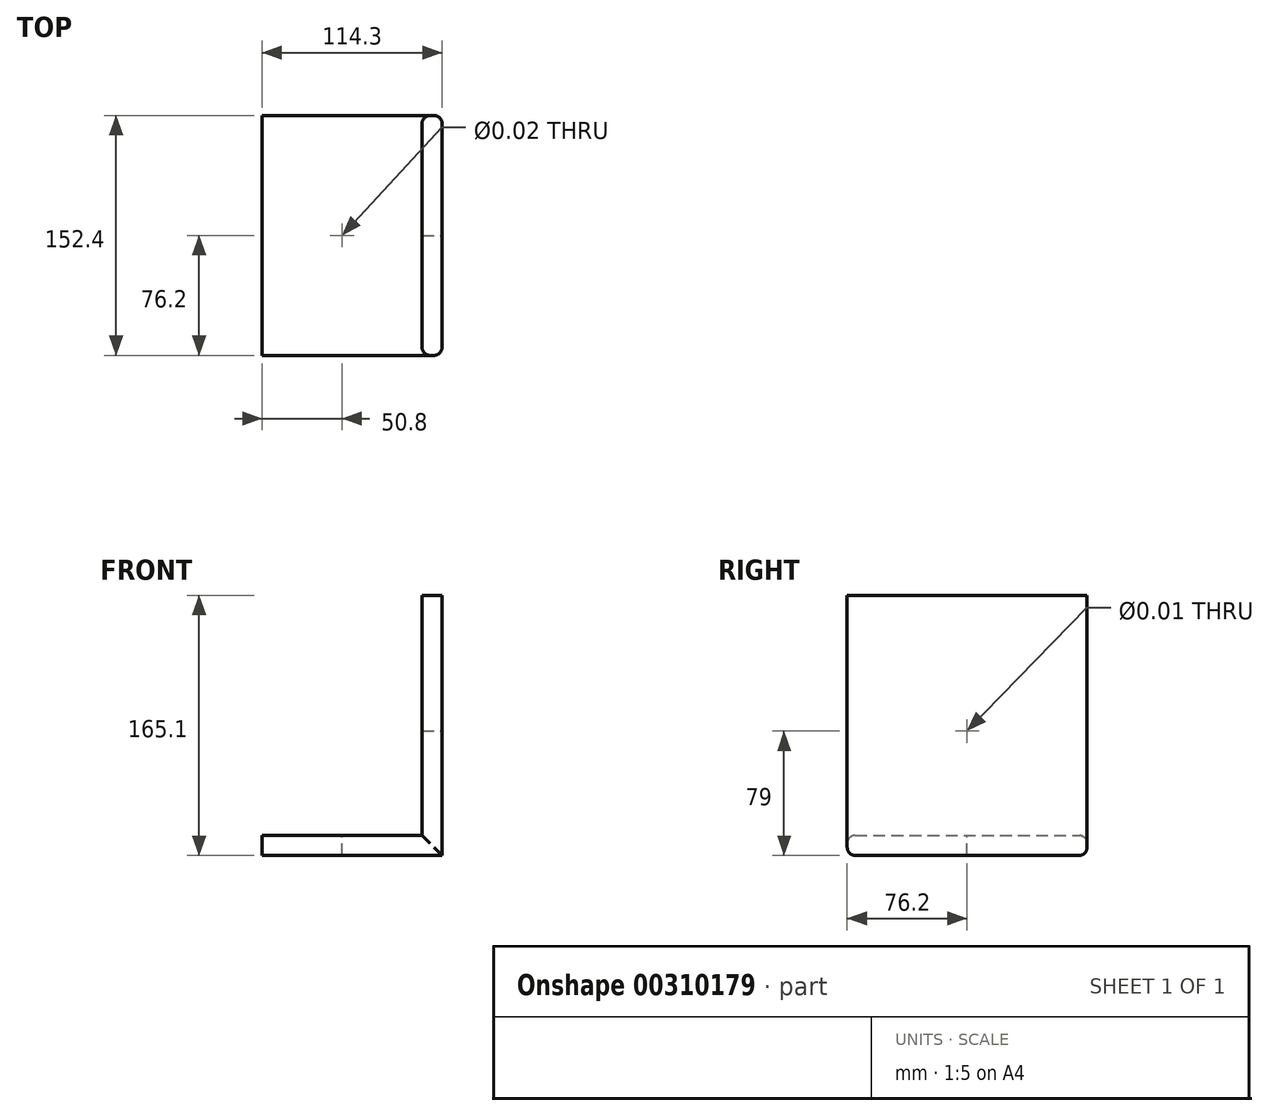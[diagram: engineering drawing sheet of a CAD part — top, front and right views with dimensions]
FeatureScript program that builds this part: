
annotation { "Feature Type Name" : "Feature", "Feature Type Description" : "" }
export const myFeature = defineFeature(function(context is Context, id is Id, definition is map)
    precondition{}
    {
        {
            var Q0;
            Q0=qCreatedBy(makeId("Front.planeOp"),FACE);
            var sketch = newSketch(context, id + "F0", { "sketchPlane" : qUnion([Q0])});
            skLineSegment(sketch, "E0", {"start": v(0, 86.1) * mm, "end": v(0, -79) * mm});
            skLineSegment(sketch, "E1", {"start": v(0, -79) * mm, "end": v(-114.3, -79) * mm});
            skLineSegment(sketch, "E2", {"start": v(-114.3, -79) * mm, "end": v(-114.3, -66.3) * mm});
            skLineSegment(sketch, "E3", {"start": v(-114.3, -66.3) * mm, "end": v(-12.7, -66.3) * mm});
            skLineSegment(sketch, "E4", {"start": v(-12.7, -66.3) * mm, "end": v(-12.7, 86.1) * mm});
            skLineSegment(sketch, "E5", {"start": v(-12.7, 86.1) * mm, "end": v(0, 86.1) * mm});
            skSolve(sketch);
        }
        {
            var Q0;
            Q0=makeQuery(id+"F0.imprint","IMPRINT",FACE,{"disambiguationData":[TD([[makeQuery(id+"F0.imprint","IMPRINT",EDGE,{"derivedFrom":sQuery(id+"F0.wireOp",EDGE,"E0")}),-1.0]])]});
            extrude(context, id + "F1", {"entities" : qUnion([Q0]), "depth" : 152.4 * mm});
        }
        {
            var Q0;
            Q0=makeQuery(id+"F1.opExtrude","SWEPT_FACE",FACE,{"disambiguationData":[OSD([sQuery(id+"F0.wireOp",EDGE,"E0")])]});
            var sketch = newSketch(context, id + "F2", { "sketchPlane" : qUnion([Q0])});
            skPoint(sketch, "E6", {"position": v(-76.2, 0) * mm});
            skPoint(sketch, "E6.positionSnap0", {"position": v(-76.2, 86.1) * mm});
            skSolve(sketch);
        }
        {
            var Q0;
            Q0=sQuery(id+"F2.wireOp",VERTEX,"E6");
            var Q1;
            Q1=makeQuery(id+"F1.opExtrude","SWEPT_BODY",BODY,{"disambiguationData":[OSD([sQuery(id+"F0.wireOp",EDGE,"E0"),sQuery(id+"F0.wireOp",EDGE,"E1"),sQuery(id+"F0.wireOp",EDGE,"E2"),sQuery(id+"F0.wireOp",EDGE,"E3"),sQuery(id+"F0.wireOp",EDGE,"E4"),sQuery(id+"F0.wireOp",EDGE,"E5")])]});
            hole(context, id + "F3", {"style" : HoleStyle.SIMPLE, "endStyle" : HoleEndStyle.THROUGH, "standardTappedOrClearance" : lookupTablePath({ "standard" : "ANSI", "size" : "3/8 (0.38)", "type" : "Drilled" }), "standardBlindInLast" : lookupTablePath({ "standard" : "ANSI", "size" : "3/8", "type" : "Drilled" }), "holeDiameter" : 3 / 203.2 * mm, "tappedDepth" : 12.7 * mm, "tapClearance" : 3, "locations" : qUnion([Q0]), "scope" : qUnion([Q1])});
        }
        {
            var Q0;
            Q0=makeQuery(id+"F1.opExtrude","SWEPT_FACE",FACE,{"disambiguationData":[OSD([sQuery(id+"F0.wireOp",EDGE,"E3")])]});
            var sketch = newSketch(context, id + "F4", { "sketchPlane" : qUnion([Q0])});
            skPoint(sketch, "E7", {"position": v(-63.5, -76.2) * mm});
            skPoint(sketch, "E7.positionSnap0", {"position": v(-63.5, -152.4) * mm});
            skPoint(sketch, "E7.positionSnap1", {"position": v(-114.3, -76.2) * mm});
            skSolve(sketch);
        }
        {
            var Q0;
            Q0=sQuery(id+"F4.wireOp",VERTEX,"E7");
            var Q1;
            Q1=makeQuery(id+"F1.opExtrude","SWEPT_BODY",BODY,{"disambiguationData":[OSD([sQuery(id+"F0.wireOp",EDGE,"E0"),sQuery(id+"F0.wireOp",EDGE,"E1"),sQuery(id+"F0.wireOp",EDGE,"E2"),sQuery(id+"F0.wireOp",EDGE,"E3"),sQuery(id+"F0.wireOp",EDGE,"E4"),sQuery(id+"F0.wireOp",EDGE,"E5")])]});
            hole(context, id + "F5", {"style" : HoleStyle.SIMPLE, "endStyle" : HoleEndStyle.THROUGH, "standardTappedOrClearance" : lookupTablePath({ "standard" : "ANSI", "size" : "1/2 (0.5)", "type" : "Drilled" }), "standardBlindInLast" : lookupTablePath({ "standard" : "ANSI", "size" : "1/2", "type" : "Drilled" }), "holeDiameter" : 1 / 50.8 * mm, "tappedDepth" : 12.7 * mm, "tapClearance" : 3, "locations" : qUnion([Q0]), "scope" : qUnion([Q1])});
        }
        {
            var Q0;
            Q0=makeQuery(id+"F1.opExtrude","CAP_EDGE",EDGE,{"disambiguationData":[OSD([sQuery(id+"F0.wireOp",EDGE,"E4")])],"isStart":false});
            var Q1;
            Q1=makeQuery(id+"F1.opExtrude","CAP_EDGE",EDGE,{"disambiguationData":[OSD([sQuery(id+"F0.wireOp",EDGE,"E3")])],"isStart":false});
            fillet(context, id + "F6", {"entities" : qUnion([Q0, Q1]), "radius" : 5.08 * mm, "tangentPropagation" : true, "allowEdgeOverflow" : false});
        }
        {
            var Q0;
            Q0=makeQuery(id+"F1.opExtrude","CAP_EDGE",EDGE,{"disambiguationData":[OSD([sQuery(id+"F0.wireOp",EDGE,"E4")])],"isStart":true});
            var Q1;
            Q1=makeQuery(id+"F1.opExtrude","CAP_EDGE",EDGE,{"disambiguationData":[OSD([sQuery(id+"F0.wireOp",EDGE,"E3")])],"isStart":true});
            fillet(context, id + "F7", {"entities" : qUnion([Q0, Q1]), "radius" : 5.08 * mm, "tangentPropagation" : true, "allowEdgeOverflow" : false});
        }
        {
            var Q0;
            Q0=makeQuery(id+"F1.opExtrude","CAP_EDGE",EDGE,{"disambiguationData":[OSD([sQuery(id+"F0.wireOp",EDGE,"E1")])],"isStart":true});
            var Q1;
            Q1=makeQuery(id+"F1.opExtrude","CAP_EDGE",EDGE,{"disambiguationData":[OSD([sQuery(id+"F0.wireOp",EDGE,"E0")])],"isStart":true});
            fillet(context, id + "F8", {"entities" : qUnion([Q0, Q1]), "radius" : 5.08 * mm, "tangentPropagation" : true, "allowEdgeOverflow" : false});
        }
        {
            var Q0;
            Q0=makeQuery(id+"F1.opExtrude","CAP_EDGE",EDGE,{"disambiguationData":[OSD([sQuery(id+"F0.wireOp",EDGE,"E1")])],"isStart":false});
            var Q1;
            Q1=makeQuery(id+"F1.opExtrude","CAP_EDGE",EDGE,{"disambiguationData":[OSD([sQuery(id+"F0.wireOp",EDGE,"E0")])],"isStart":false});
            fillet(context, id + "F9", {"entities" : qUnion([Q0, Q1]), "radius" : 5.08 * mm, "tangentPropagation" : true, "allowEdgeOverflow" : false});
        }
    });
